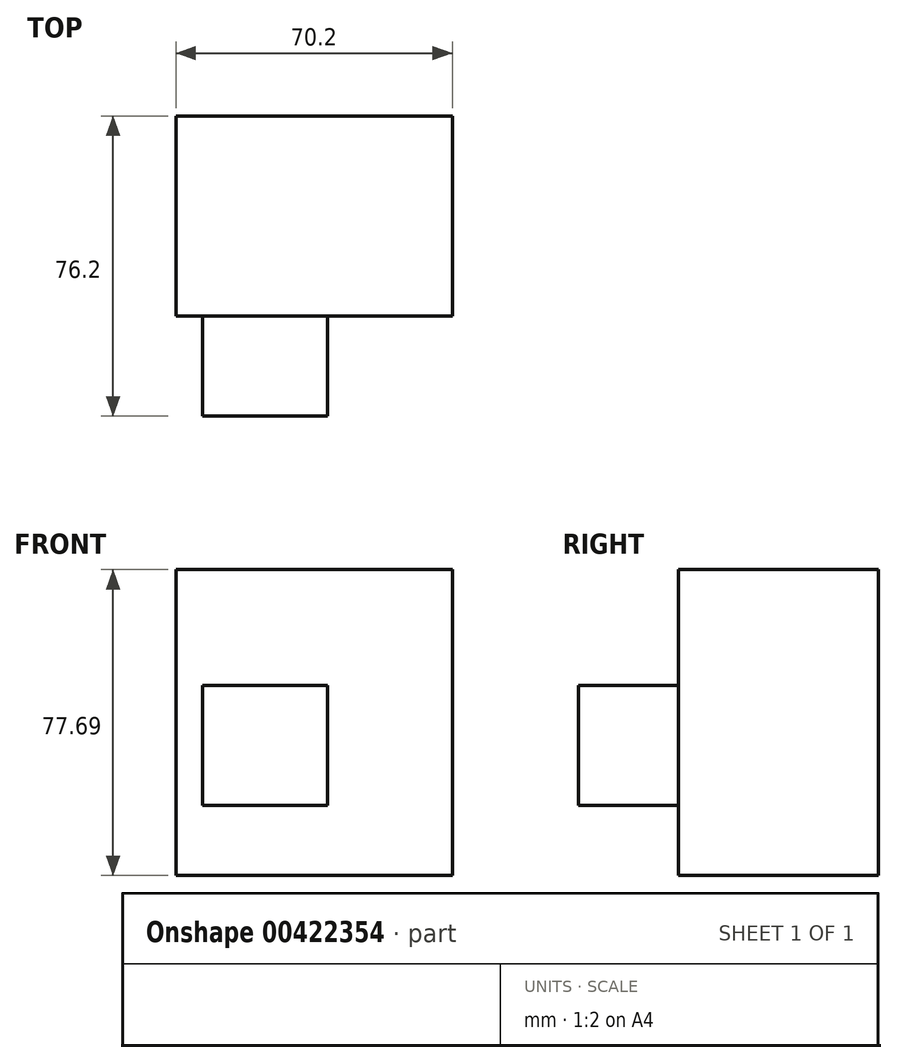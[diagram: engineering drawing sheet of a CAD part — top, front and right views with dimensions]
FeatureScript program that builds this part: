
annotation { "Feature Type Name" : "Feature", "Feature Type Description" : "" }
export const myFeature = defineFeature(function(context is Context, id is Id, definition is map)
    precondition{}
    {
        {
            var Q0;
            Q0=qCreatedBy(makeId("Front.planeOp"),FACE);
            var sketch = newSketch(context, id + "F0", { "sketchPlane" : qUnion([Q0])});
            skLineSegment(sketch, "E0.bottom", {"start": v(-48, 27.62) * mm, "end": v(-6.2, 27.62) * mm});
            skLineSegment(sketch, "E0.top", {"start": v(-48, -11.61) * mm, "end": v(-6.2, -11.61) * mm});
            skLineSegment(sketch, "E0.left", {"start": v(-48, 27.62) * mm, "end": v(-48, -11.61) * mm});
            skLineSegment(sketch, "E0.right", {"start": v(-6.2, 27.62) * mm, "end": v(-6.2, -11.61) * mm});
            skLineSegment(sketch, "E1.bottom", {"start": v(-51.62, 56.78) * mm, "end": v(18.58, 56.78) * mm});
            skLineSegment(sketch, "E1.top", {"start": v(-51.62, -20.9) * mm, "end": v(18.58, -20.9) * mm});
            skLineSegment(sketch, "E1.left", {"start": v(-51.62, 56.78) * mm, "end": v(-51.62, -20.9) * mm});
            skLineSegment(sketch, "E1.right", {"start": v(18.58, 56.78) * mm, "end": v(18.58, -20.9) * mm});
            skSolve(sketch);
        }
        {
            var Q0;
            Q0 = qSketchRegion(id + "F0", true);
            var Q1;
            Q1=makeQuery(id+"F0.imprint","IMPRINT",FACE,{"disambiguationData":[TD([[makeQuery(id+"F0.imprint","IMPRINT",EDGE,{"derivedFrom":sQuery(id+"F0.wireOp",EDGE,"E0.bottom")}),-1.0]])]});
            extrude(context, id + "F1", {"entities" : qUnion([Q0, Q1]), "oppositeDirection" : true, "depth" : 50.8 * mm});
        }
        {
            var Q0;
            Q0=makeQuery(id+"F1.opExtrude","CAP_FACE",FACE,{"disambiguationData":[OSD([sQuery(id+"F0.wireOp",EDGE,"E1.bottom"),sQuery(id+"F0.wireOp",EDGE,"E1.top"),sQuery(id+"F0.wireOp",EDGE,"E1.left"),sQuery(id+"F0.wireOp",EDGE,"E1.right")])],"isStart":true});
            var sketch = newSketch(context, id + "F2", { "sketchPlane" : qUnion([Q0])});
            skLineSegment(sketch, "E2.bottom", {"start": v(-44.9, 27.36) * mm, "end": v(-13.16, 27.36) * mm});
            skLineSegment(sketch, "E2.top", {"start": v(-44.9, -3.1) * mm, "end": v(-13.16, -3.1) * mm});
            skLineSegment(sketch, "E2.left", {"start": v(-44.9, 27.36) * mm, "end": v(-44.9, -3.1) * mm});
            skLineSegment(sketch, "E2.right", {"start": v(-13.16, 27.36) * mm, "end": v(-13.16, -3.1) * mm});
            skSolve(sketch);
        }
        {
            var Q0;
            Q0 = qSketchRegion(id + "F2", true);
            extrude(context, id + "F3", {"entities" : qUnion([Q0]), "operationType" : NewBodyOperationType.ADD, "depth" : 25.4 * mm});
        }
    });
